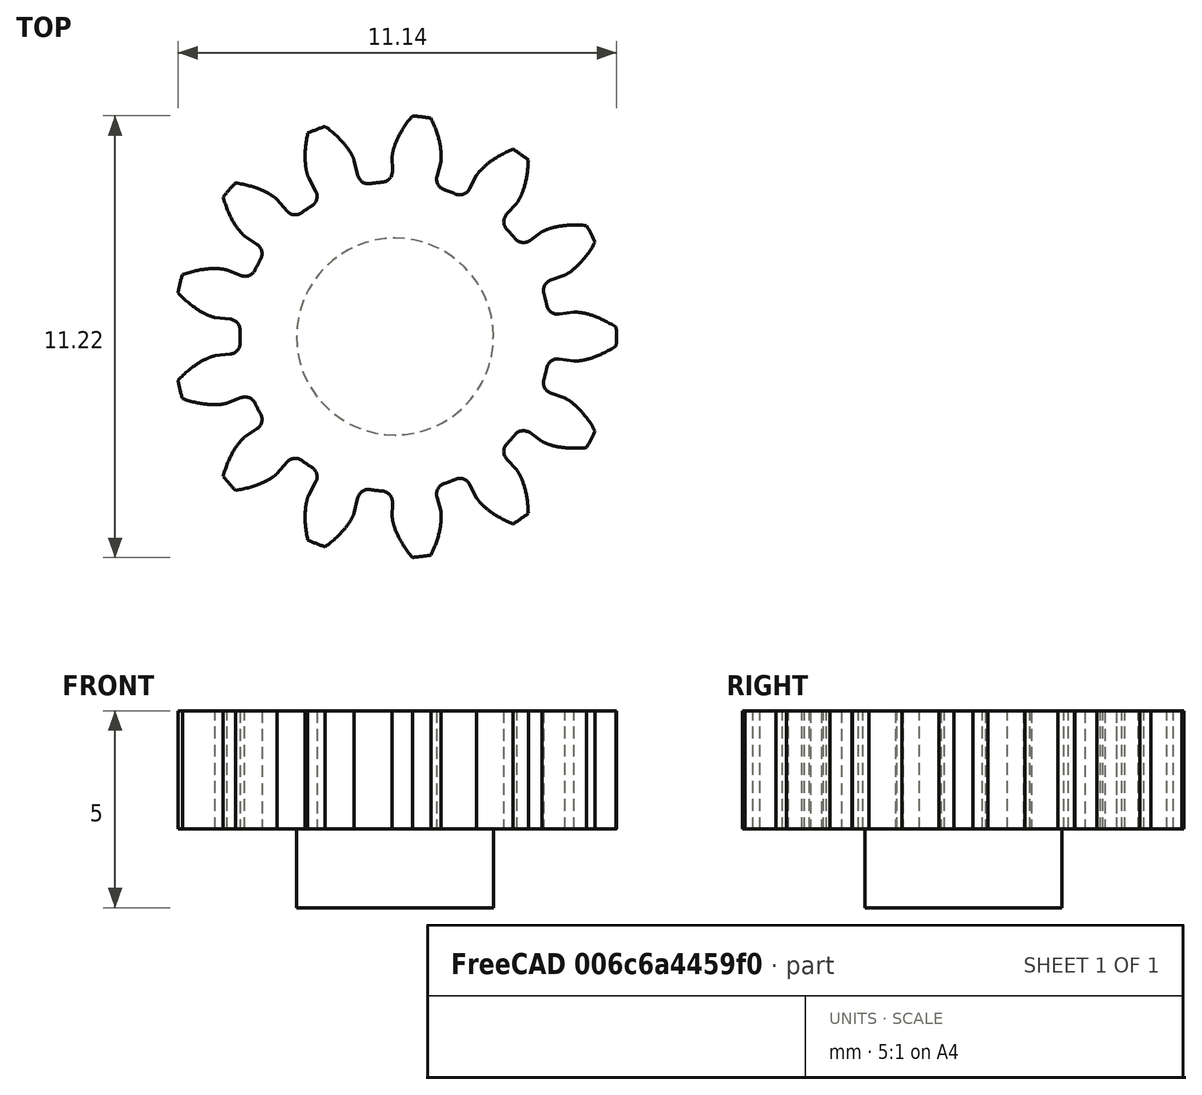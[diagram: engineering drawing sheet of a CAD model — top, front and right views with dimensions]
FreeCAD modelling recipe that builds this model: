
FCSTD DOCUMENT  (FreeCAD 0.17R13541 (Git))
Label: laser_sledge__driving_gear_2
License: All rights reserved
LicenseURL: http://en.wikipedia.org/wiki/All_rights_reserved
objects: PartDesign::Pad×2, Part::Part2DObjectPython×1, Sketcher::SketchObject×1, PartDesign::Body×1, Fem::FemMeshObjectPython×1, Mesh::Feature×1
note: 7 computed .brp shape members not serialized (recipe doc carries the construction recipe); baked Part::Feature solids carry a one-line shape summary decoded from their .brp

FEATURE [Part::Part2DObjectPython] InvoluteGear  # Draft 2D object (typed FeaturePython)
  ExternalGear = true
  HighPrecision = true
  Modules = 0.75
  NumberOfTeeth = 13
  PressureAngle = 20
FEATURE [Sketcher::SketchObject] Sketch
  MapMode = 5
  Support = -> [XY_Plane]
  sketch-geometry (1):
    g0: Circle CenterX=0 CenterY=0 CenterZ=0 NormalX=0 NormalY=0 NormalZ=1 AngleXU=0 Radius=2.5
  constraints (2):
    c: Coincident(g0,g-1)
    c: Radius(g0) = 2.5
FEATURE [PartDesign::Pad] Pad
  Length = 3
  Length2 = 100
  Profile = -> InvoluteGear
  Type = 0
FEATURE [PartDesign::Pad] Pad001
  BaseFeature = -> Pad
  Length = 2
  Length2 = 100
  Profile = -> Sketch
  Reversed = true
  Type = 0
FEATURE [PartDesign::Body] Body
  Group = -> [Sketch,InvoluteGear,Pad,Pad001]
  Origin = -> Origin
  Tip = -> Pad001
FEATURE [Fem::FemMeshObjectPython] FEMMeshGmsh  # FEM object (typed FeaturePython)
  Algorithm2D = 0
  Algorithm3D = 0
  CharacteristicLengthMax = 0.5
  CharacteristicLengthMin = 0.1
  CoherenceMesh = true
  ElementDimension = 0
  ElementOrder = 1
  GeometryTolerance = 1e-06
  GroupsOfNodes = false
  HighOrderOptimize = false
  OptimizeNetgen = false
  OptimizeStd = true
  Part = -> Pad001
  RecombineAll = false
FEATURE [Mesh::Feature] Mesh
